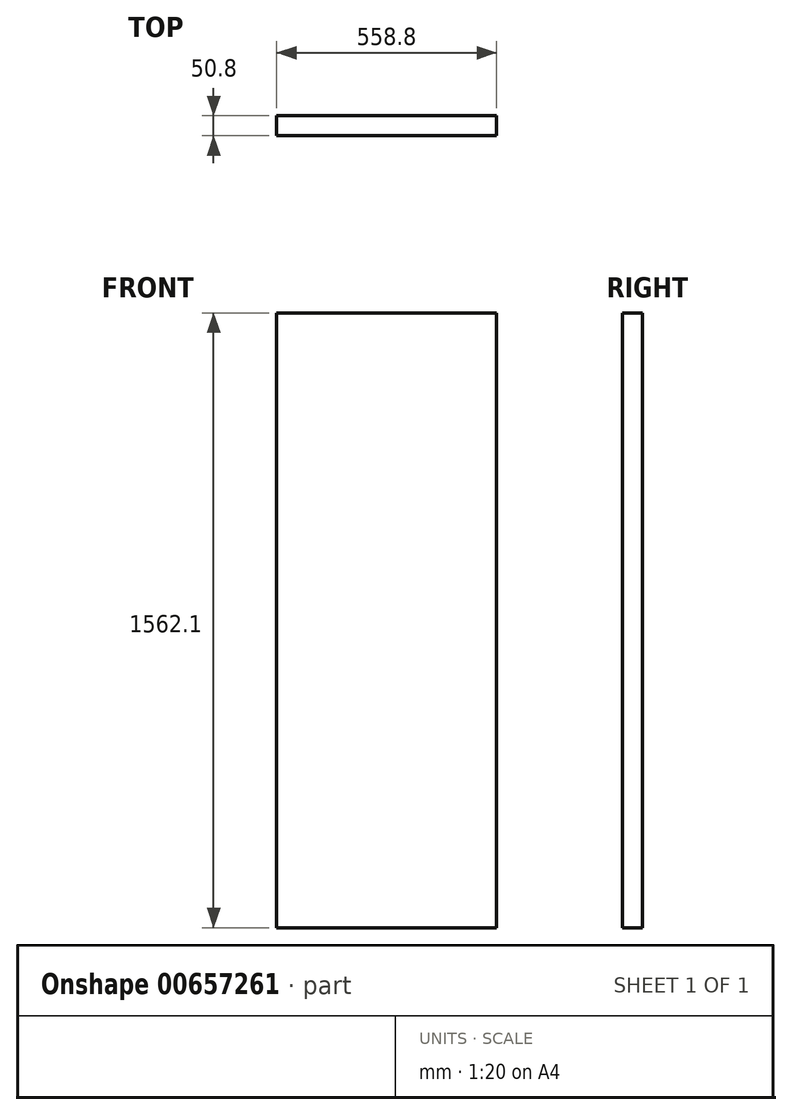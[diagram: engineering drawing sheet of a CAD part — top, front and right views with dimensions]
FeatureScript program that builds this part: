
annotation { "Feature Type Name" : "Feature", "Feature Type Description" : "" }
export const myFeature = defineFeature(function(context is Context, id is Id, definition is map)
    precondition{}
    {
        {
            var Q0;
            Q0=qCreatedBy(makeId("Front.planeOp"),FACE);
            var sketch = newSketch(context, id + "F0", { "sketchPlane" : qUnion([Q0])});
            skLineSegment(sketch, "E0.bottom", {"start": v(-279.4, 781.05) * mm, "end": v(279.4, 781.05) * mm});
            skLineSegment(sketch, "E0.top", {"start": v(-279.4, -781.05) * mm, "end": v(279.4, -781.05) * mm});
            skLineSegment(sketch, "E0.left", {"start": v(-279.4, 781.05) * mm, "end": v(-279.4, -781.05) * mm});
            skLineSegment(sketch, "E0.right", {"start": v(279.4, 781.05) * mm, "end": v(279.4, -781.05) * mm});
            skSolve(sketch);
        }
        {
            var Q0;
            Q0=qSketchRegion(id+"F0",true);
            extrude(context, id + "F1", {"entities" : qUnion([Q0]), "depth" : 50.8 * mm, "offsetDistance" : 25.4 * mm});
        }
    });
